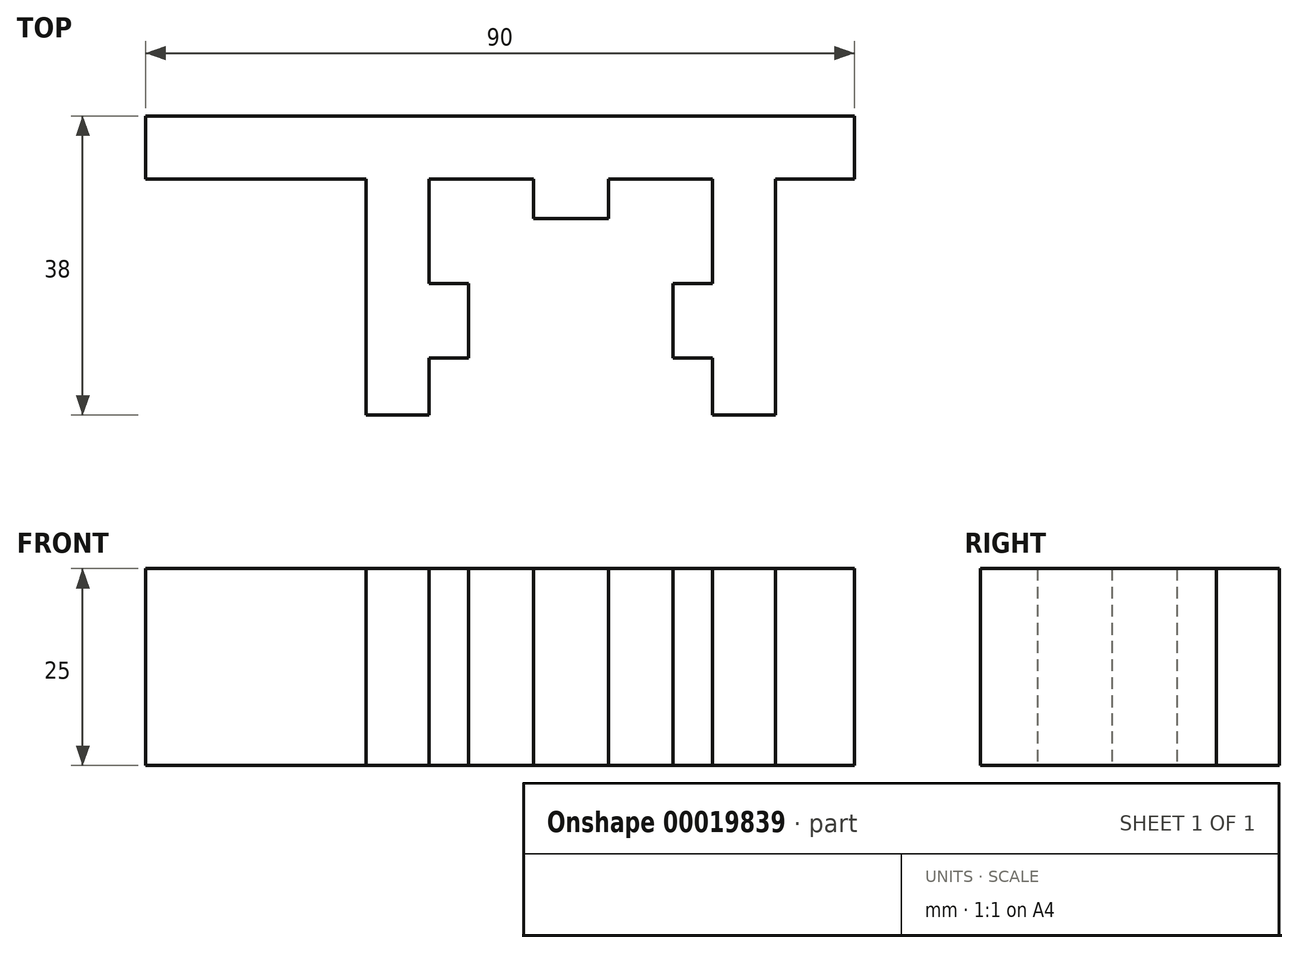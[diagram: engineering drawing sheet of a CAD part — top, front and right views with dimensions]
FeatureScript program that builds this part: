
annotation { "Feature Type Name" : "Feature", "Feature Type Description" : "" }
export const myFeature = defineFeature(function(context is Context, id is Id, definition is map)
    precondition{}
    {
        {
            var Q0;
            Q0=qCreatedBy(makeId("Top.planeOp"),FACE);
            var sketch = newSketch(context, id + "F0", { "sketchPlane" : qUnion([Q0])});
            skLineSegment(sketch, "E0", {"start": v(0, 0) * mm, "end": v(0, 30) * mm});
            skLineSegment(sketch, "E1", {"start": v(0, 30) * mm, "end": v(-28, 30) * mm});
            skLineSegment(sketch, "E2", {"start": v(-28, 30) * mm, "end": v(-28, 38) * mm});
            skLineSegment(sketch, "E3", {"start": v(-28, 38) * mm, "end": v(62, 38) * mm});
            skLineSegment(sketch, "E4", {"start": v(62, 38) * mm, "end": v(62, 30) * mm});
            skLineSegment(sketch, "E5", {"start": v(62, 30) * mm, "end": v(52, 30) * mm});
            skLineSegment(sketch, "E6", {"start": v(52, 30) * mm, "end": v(52, 0) * mm});
            skLineSegment(sketch, "E7", {"start": v(52, 0) * mm, "end": v(44, 0) * mm});
            skLineSegment(sketch, "E8", {"start": v(44, 0) * mm, "end": v(44, 7.25) * mm});
            skLineSegment(sketch, "E9", {"start": v(44, 7.25) * mm, "end": v(39, 7.25) * mm});
            skLineSegment(sketch, "E10", {"start": v(39, 7.25) * mm, "end": v(39, 16.75) * mm});
            skLineSegment(sketch, "E11", {"start": v(39, 16.75) * mm, "end": v(44, 16.75) * mm});
            skLineSegment(sketch, "E12", {"start": v(44, 16.75) * mm, "end": v(44, 30) * mm});
            skLineSegment(sketch, "E13", {"start": v(44, 30) * mm, "end": v(30.75, 30) * mm});
            skLineSegment(sketch, "E14", {"start": v(30.75, 30) * mm, "end": v(30.75, 25) * mm});
            skLineSegment(sketch, "E15", {"start": v(30.75, 25) * mm, "end": v(21.25, 25) * mm});
            skLineSegment(sketch, "E16", {"start": v(21.25, 25) * mm, "end": v(21.25, 30) * mm});
            skLineSegment(sketch, "E17", {"start": v(21.25, 30) * mm, "end": v(8, 30) * mm});
            skLineSegment(sketch, "E18", {"start": v(8, 30) * mm, "end": v(8, 16.75) * mm});
            skLineSegment(sketch, "E19", {"start": v(8, 16.75) * mm, "end": v(13, 16.75) * mm});
            skLineSegment(sketch, "E20", {"start": v(13, 16.75) * mm, "end": v(13, 7.25) * mm});
            skLineSegment(sketch, "E21", {"start": v(13, 7.25) * mm, "end": v(8, 7.25) * mm});
            skLineSegment(sketch, "E22", {"start": v(8, 7.25) * mm, "end": v(8, 0) * mm});
            skLineSegment(sketch, "E23", {"start": v(8, 0) * mm, "end": v(0, 0) * mm});
            skSolve(sketch);
        }
        {
            var Q0;
            Q0=makeQuery(id+"F0.imprint","IMPRINT",FACE,{"disambiguationData":[TD([[makeQuery(id+"F0.imprint","IMPRINT",EDGE,{"derivedFrom":sQuery(id+"F0.wireOp",EDGE,"E0")}),-1.0]])]});
            extrude(context, id + "F1", {"entities" : qUnion([Q0]), "depth" : 25 * mm});
        }
    });
